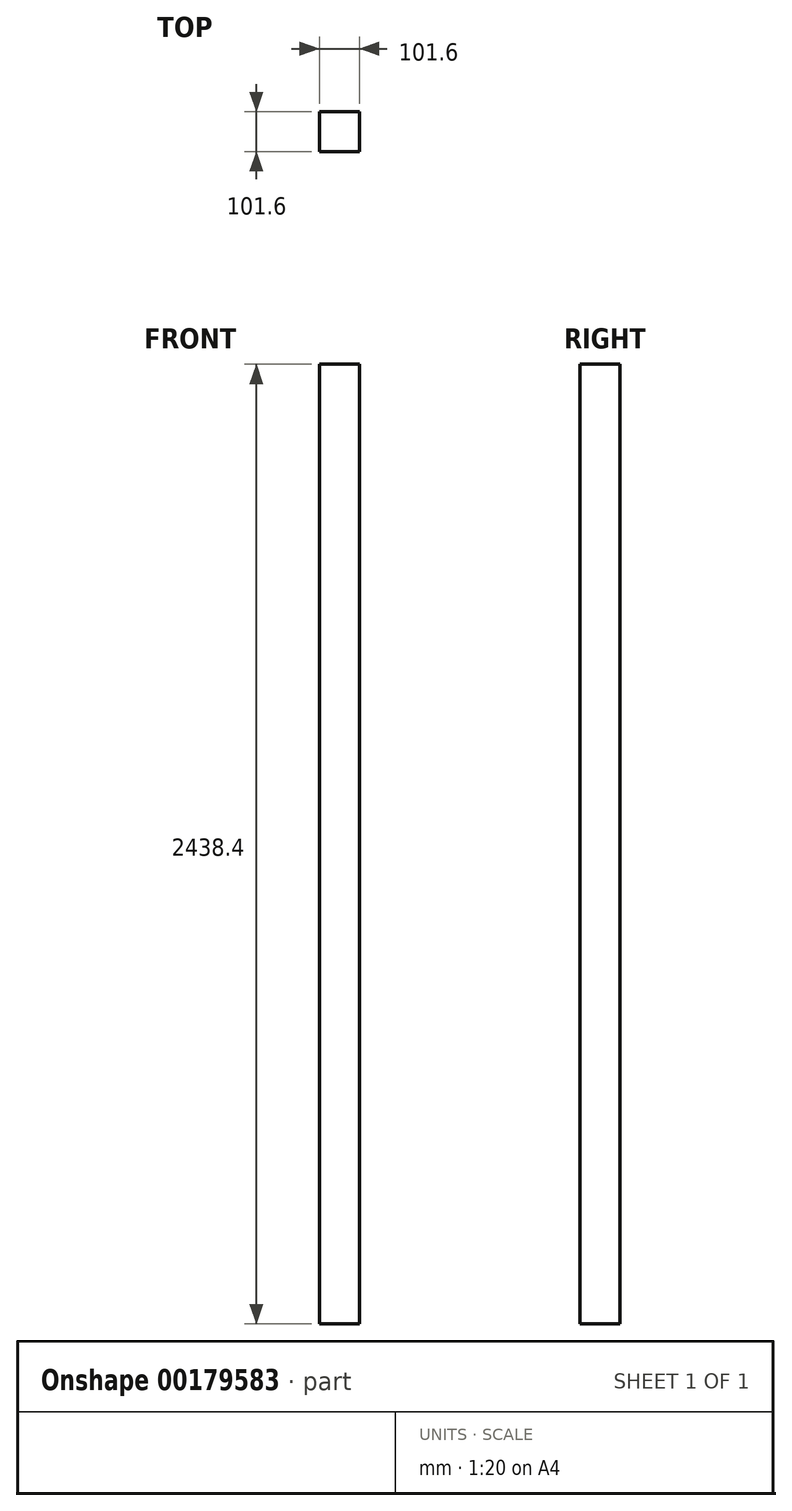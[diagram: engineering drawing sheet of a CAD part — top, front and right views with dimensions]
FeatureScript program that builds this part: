
annotation { "Feature Type Name" : "Feature", "Feature Type Description" : "" }
export const myFeature = defineFeature(function(context is Context, id is Id, definition is map)
    precondition{}
    {
        {
            var Q0;
            Q0=qCreatedBy(makeId("Top.planeOp"),FACE);
            var sketch = newSketch(context, id + "F0", { "sketchPlane" : qUnion([Q0])});
            skLineSegment(sketch, "E0.bottom", {"start": v(142.56, -54.23) * mm, "end": v(244.16, -54.23) * mm});
            skLineSegment(sketch, "E0.top", {"start": v(142.56, -155.83) * mm, "end": v(244.16, -155.83) * mm});
            skLineSegment(sketch, "E0.left", {"start": v(142.56, -54.23) * mm, "end": v(142.56, -155.83) * mm});
            skLineSegment(sketch, "E0.right", {"start": v(244.16, -54.23) * mm, "end": v(244.16, -155.83) * mm});
            skSolve(sketch);
        }
        {
            var Q0;
            Q0 = qSketchRegion(id + "F0", true);
            extrude(context, id + "F1", {"entities" : qUnion([Q0]), "depth" : 2438.4 * mm});
        }
    });
